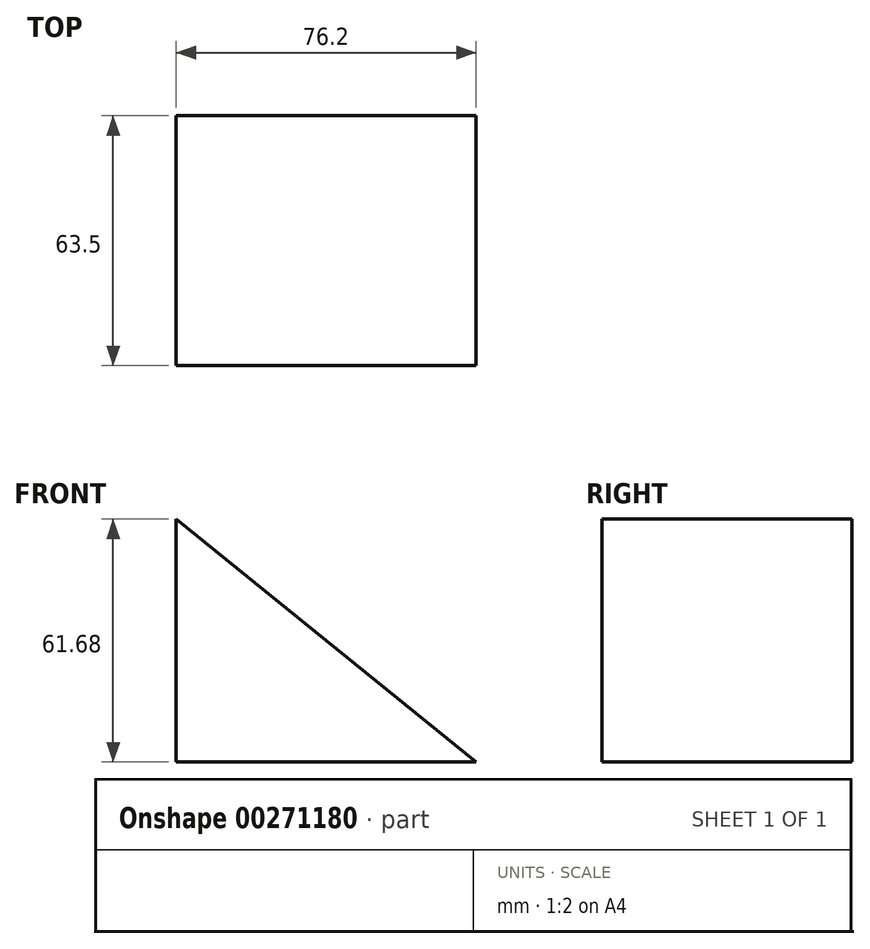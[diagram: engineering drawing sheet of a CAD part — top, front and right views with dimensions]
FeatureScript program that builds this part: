
annotation { "Feature Type Name" : "Feature", "Feature Type Description" : "" }
export const myFeature = defineFeature(function(context is Context, id is Id, definition is map)
    precondition{}
    {
        {
            var Q0;
            Q0=qCreatedBy(makeId("Front.planeOp"),FACE);
            var sketch = newSketch(context, id + "F0", { "sketchPlane" : qUnion([Q0])});
            skLineSegment(sketch, "E0", {"start": v(0, 0) * mm, "end": v(0, 61.68) * mm});
            skLineSegment(sketch, "E1", {"start": v(0, 61.68) * mm, "end": v(76.2, 0) * mm});
            skLineSegment(sketch, "E2", {"start": v(76.2, 0) * mm, "end": v(0, 0) * mm});
            skSolve(sketch);
        }
        {
            var Q0;
            Q0 = qSketchRegion(id + "F0", true);
            extrude(context, id + "F1", {"entities" : qUnion([Q0]), "depth" : 63.5 * mm});
        }
    });
